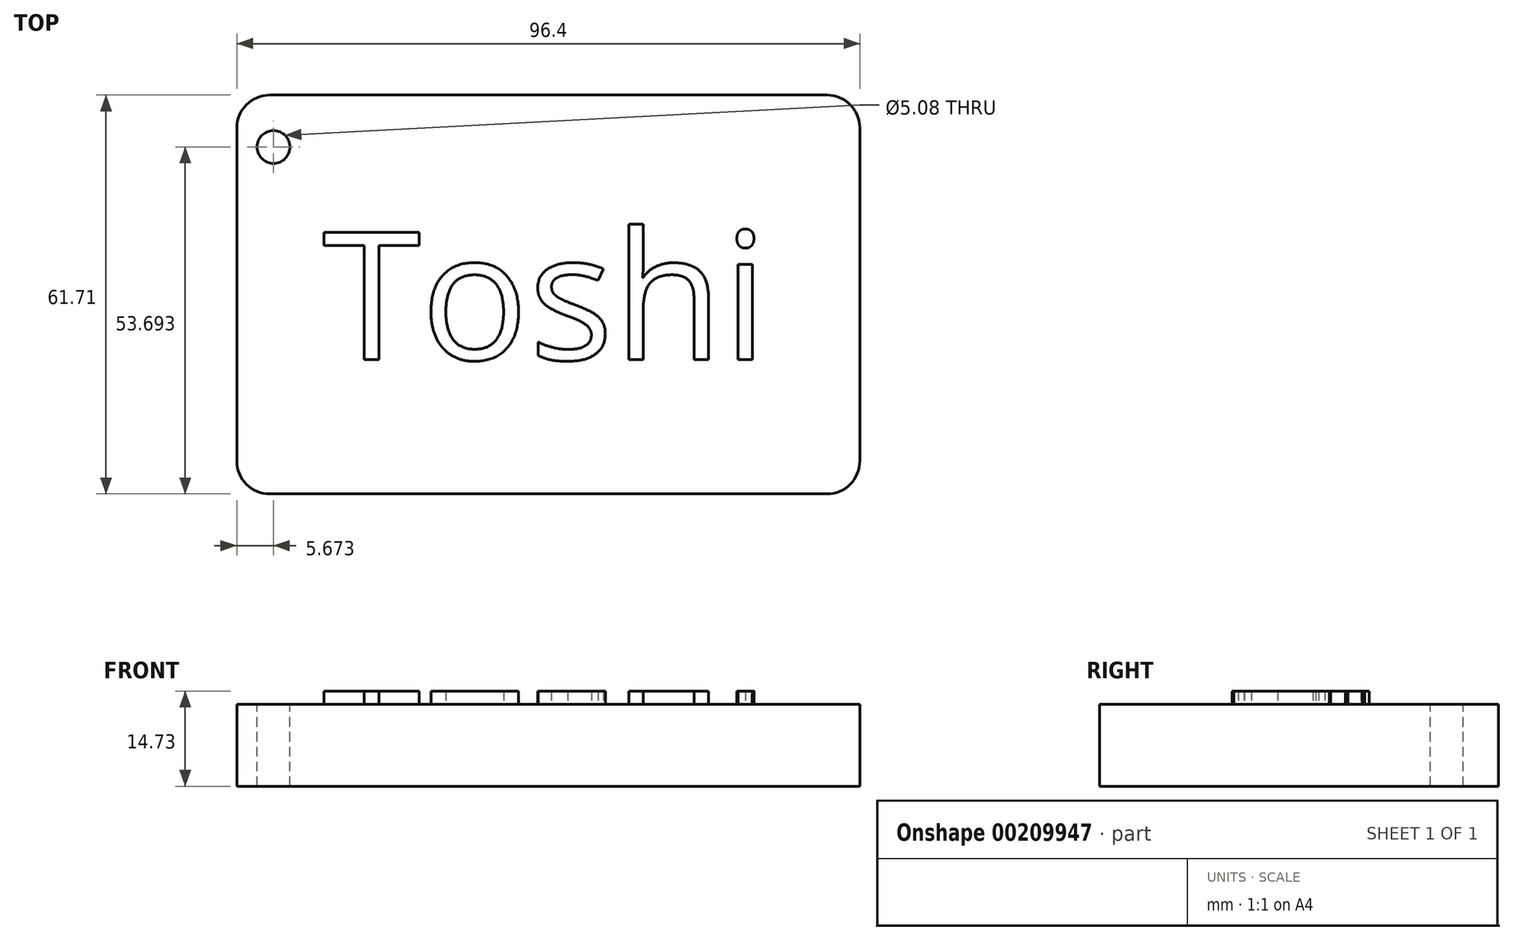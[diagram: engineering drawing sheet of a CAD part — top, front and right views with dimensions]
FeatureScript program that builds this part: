
annotation { "Feature Type Name" : "Feature", "Feature Type Description" : "" }
export const myFeature = defineFeature(function(context is Context, id is Id, definition is map)
    precondition{}
    {
        {
            var Q0;
            Q0=qCreatedBy(makeId("Top.planeOp"),FACE);
            var sketch = newSketch(context, id + "F0", { "sketchPlane" : qUnion([Q0])});
            skLineSegment(sketch, "E0.bottom", {"start": v(-47.24, 30.33) * mm, "end": v(49.16, 30.33) * mm});
            skLineSegment(sketch, "E0.top", {"start": v(-47.24, -31.38) * mm, "end": v(49.16, -31.38) * mm});
            skLineSegment(sketch, "E0.left", {"start": v(-47.24, 30.33) * mm, "end": v(-47.24, -31.38) * mm});
            skLineSegment(sketch, "E0.right", {"start": v(49.16, 30.33) * mm, "end": v(49.16, -31.38) * mm});
            skSolve(sketch);
        }
        {
            var Q0;
            Q0 = qSketchRegion(id + "F0", true);
            extrude(context, id + "F1", {"entities" : qUnion([Q0]), "depth" : 12.7 * mm});
        }
        {
            var Q0;
            Q0=makeQuery(id+"F1.opExtrude","CAP_FACE",FACE,{"disambiguationData":[OSD([sQuery(id+"F0.wireOp",EDGE,"E0.bottom"),sQuery(id+"F0.wireOp",EDGE,"E0.top"),sQuery(id+"F0.wireOp",EDGE,"E0.left"),sQuery(id+"F0.wireOp",EDGE,"E0.right")])],"isStart":false});
            var sketch = newSketch(context, id + "F2", { "sketchPlane" : qUnion([Q0])});
            skText(sketch, "E1", { "text": "Toshi", "fontName": "OpenSans-Regular.ttf"});
            const initialGuessF2  = {"E1": [-0.034, -0.0106, 1, 0, 0.01984]};
            skSetInitialGuess(sketch, initialGuessF2);
            skSolve(sketch);
        }
        {
            var Q0;
            Q0 = qSketchRegion(id + "F2", true);
            extrude(context, id + "F3", {"entities" : qUnion([Q0]), "operationType" : NewBodyOperationType.ADD, "depth" : 2.03 * mm});
        }
        {
            var Q0;
            {var subQ0=sQuery(id+"F0.wireOp",EDGE,"E0.left");var subQ1=sQuery(id+"F0.wireOp",EDGE,"E0.top");var subQ2=sQuery(id+"F0.wireOp",EDGE,"E0.right");var subQ3=sQuery(id+"F0.wireOp",EDGE,"E0.bottom");Q0=makeQuery(id+"F3.boolean.opBoolean","SPLIT",FACE,{"disambiguationData":[TD([makeQuery(id+"F1.opExtrude","SWEPT_FACE",FACE,{"disambiguationData":[OSD([subQ3])]})])],"derivedFrom":makeQuery(id+"F1.opExtrude","CAP_FACE",FACE,{"disambiguationData":[OSD([subQ3,subQ1,subQ0,subQ2])],"isStart":false})});}
            var sketch = newSketch(context, id + "F4", { "sketchPlane" : qUnion([Q0])});
            skCircle(sketch, "E2", {"center": v(-41.57, 22.31) * mm, "radius": 3.67 * mm});
            skSolve(sketch);
        }
        {
            var Q0;
            Q0=sQuery(id+"F4.wireOp",VERTEX,"E2.center");
            var Q1;
            Q1=makeQuery(id+"F1.opExtrude","SWEPT_BODY",BODY,{"disambiguationData":[OSD([sQuery(id+"F0.wireOp",EDGE,"E0.bottom"),sQuery(id+"F0.wireOp",EDGE,"E0.top"),sQuery(id+"F0.wireOp",EDGE,"E0.left"),sQuery(id+"F0.wireOp",EDGE,"E0.right")])]});
            hole(context, id + "F5", {"style" : HoleStyle.SIMPLE, "endStyle" : HoleEndStyle.THROUGH, "holeDiameter" : 5.08 * mm, "locations" : qUnion([Q0]), "scope" : qUnion([Q1]), "isTappedThrough" : true});
        }
        {
            var Q0;
            Q0=makeQuery(id+"F1.opExtrude","CAP_FACE",FACE,{"disambiguationData":[OSD([sQuery(id+"F0.wireOp",EDGE,"E0.bottom"),sQuery(id+"F0.wireOp",EDGE,"E0.top"),sQuery(id+"F0.wireOp",EDGE,"E0.left"),sQuery(id+"F0.wireOp",EDGE,"E0.right")])],"isStart":true});
            var sketch = newSketch(context, id + "F6", { "sketchPlane" : qUnion([Q0])});
            skSolve(sketch);
        }
        {
            var Q0;
            Q0=makeQuery(id+"F1.opExtrude","SWEPT_EDGE",EDGE,{"disambiguationData":[OSD([sQuery(id+"F0.wireOp",EDGE,"E0.top"),sQuery(id+"F0.wireOp",EDGE,"E0.left")])]});
            fillet(context, id + "F7", {"entities" : qUnion([Q0]), "radius" : 5.08 * mm, "tangentPropagation" : true, "allowEdgeOverflow" : false});
        }
        {
            var Q0;
            Q0=makeQuery(id+"F1.opExtrude","SWEPT_EDGE",EDGE,{"disambiguationData":[OSD([sQuery(id+"F0.wireOp",EDGE,"E0.bottom"),sQuery(id+"F0.wireOp",EDGE,"E0.left")])]});
            var Q1;
            {var subQ0=sQuery(id+"F0.wireOp",EDGE,"E0.left");Q1=makeQuery(id+"F7.opFillet","BLEND_EDGE",EDGE,{"blendedFrom":[makeQuery(id+"F1.opExtrude","SWEPT_EDGE",EDGE,{"disambiguationData":[OSD([sQuery(id+"F0.wireOp",EDGE,"E0.top"),subQ0])]}),makeQuery(id+"F1.opExtrude","SWEPT_FACE",FACE,{"disambiguationData":[OSD([subQ0])]})],"blendedInto":[makeQuery(id+"F1.opExtrude","SWEPT_FACE",FACE,{"disambiguationData":[OSD([subQ0])]})]});}
            var Q2;
            Q2=makeQuery(id+"F1.opExtrude","SWEPT_EDGE",EDGE,{"disambiguationData":[OSD([sQuery(id+"F0.wireOp",EDGE,"E0.bottom"),sQuery(id+"F0.wireOp",EDGE,"E0.right")])]});
            var Q3;
            Q3=makeQuery(id+"F1.opExtrude","SWEPT_EDGE",EDGE,{"disambiguationData":[OSD([sQuery(id+"F0.wireOp",EDGE,"E0.top"),sQuery(id+"F0.wireOp",EDGE,"E0.right")])]});
            fillet(context, id + "F8", {"entities" : qUnion([Q0, Q1, Q2, Q3]), "radius" : 5.08 * mm, "tangentPropagation" : true, "allowEdgeOverflow" : false});
        }
    });
